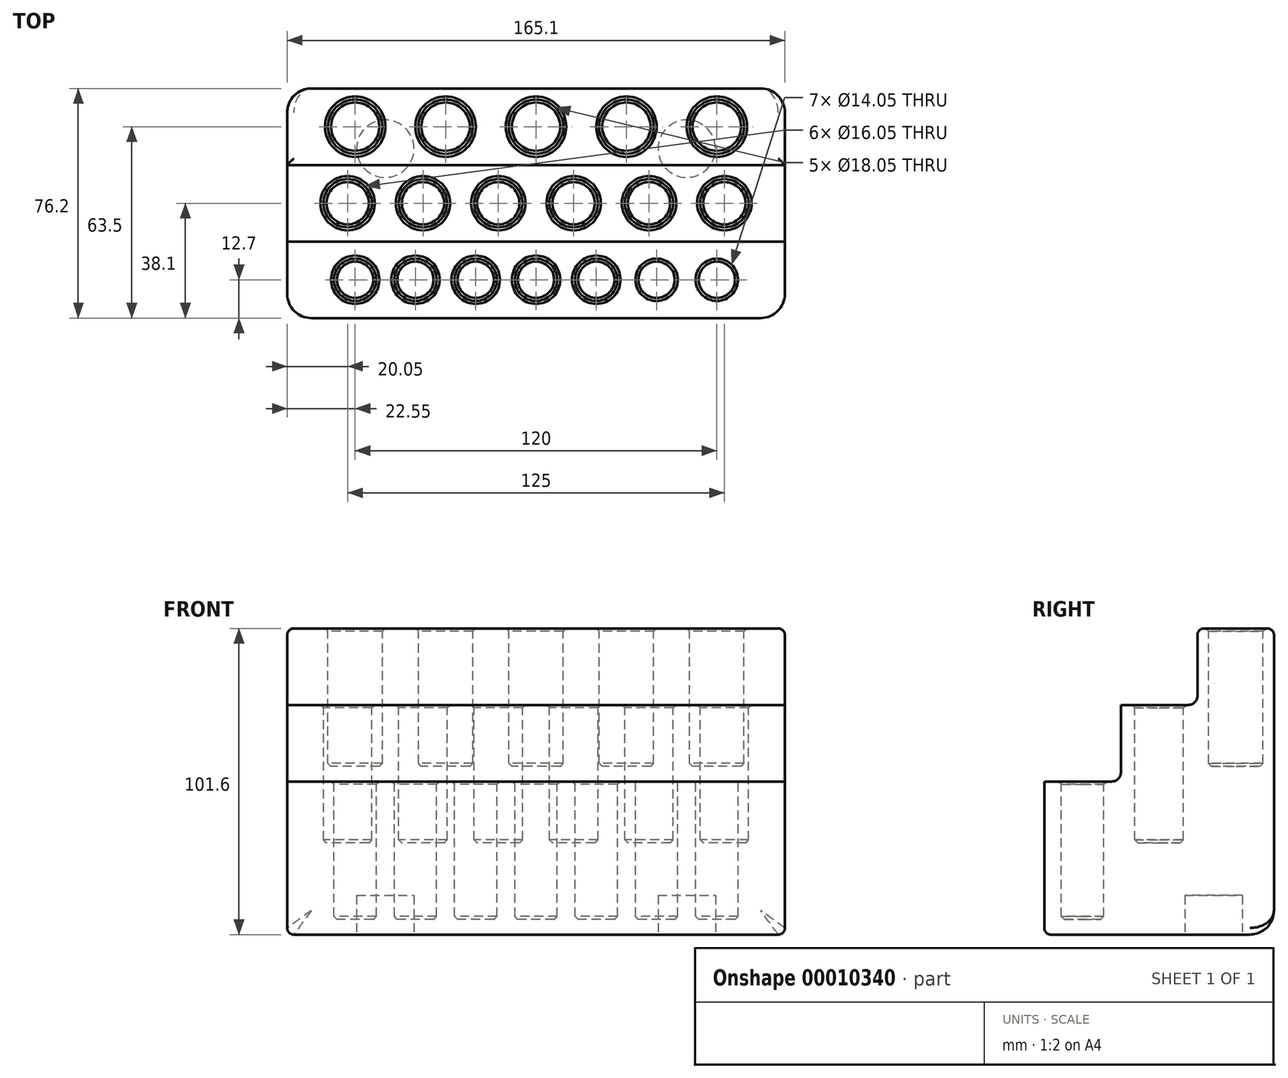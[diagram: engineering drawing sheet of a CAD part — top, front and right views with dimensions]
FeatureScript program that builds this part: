
annotation { "Feature Type Name" : "Feature", "Feature Type Description" : "" }
export const myFeature = defineFeature(function(context is Context, id is Id, definition is map)
    precondition{}
    {
        {
            var Q0;
            Q0=qCreatedBy(makeId("Top.planeOp"),FACE);
            var sketch = newSketch(context, id + "F0", { "sketchPlane" : qUnion([Q0])});
            skLineSegment(sketch, "E0.bottom", {"start": v(-77.55, 38.1) * mm, "end": v(77.55, 38.1) * mm});
            skLineSegment(sketch, "E0.top", {"start": v(-77.55, -38.1) * mm, "end": v(77.55, -38.1) * mm});
            skLineSegment(sketch, "E0.left", {"start": v(-82.55, 33.1) * mm, "end": v(-82.55, -33.1) * mm});
            skLineSegment(sketch, "E0.right", {"start": v(82.55, 33.1) * mm, "end": v(82.55, -33.1) * mm});
            skPoint(sketch, "E1.visualSharp", {"position": v(-82.55, 38.1) * mm});
            skPoint(sketch, "E2.visualSharp", {"position": v(82.55, -38.1) * mm});
            skPoint(sketch, "E3.visualSharp", {"position": v(-82.55, -38.1) * mm});
            skLineSegment(sketch, "E4", {"start": v(0, 38.1) * mm, "end": v(0, -38.1) * mm});
            skLineSegment(sketch, "E5", {"start": v(0, -38.1) * mm, "end": v(0, 0) * mm});
            skLineSegment(sketch, "E6", {"start": v(-82.55, 0) * mm, "end": v(0, 0) * mm});
            skLineSegment(sketch, "E7", {"start": v(82.55, 0) * mm, "end": v(0, 0) * mm});
            skLineSegment(sketch, "E8", {"start": v(-82.55, 33.1) * mm, "end": v(-82.55, 38.1) * mm});
            skLineSegment(sketch, "E9", {"start": v(-77.55, 38.1) * mm, "end": v(-82.55, 38.1) * mm});
            skLineSegment(sketch, "E10", {"start": v(77.55, 38.1) * mm, "end": v(82.55, 38.1) * mm});
            skLineSegment(sketch, "E11", {"start": v(82.55, 33.1) * mm, "end": v(82.55, 38.1) * mm});
            skLineSegment(sketch, "E12", {"start": v(-82.55, -33.1) * mm, "end": v(-82.55, -38.1) * mm});
            skLineSegment(sketch, "E13", {"start": v(-82.55, -38.1) * mm, "end": v(-77.55, -38.1) * mm});
            skLineSegment(sketch, "E14", {"start": v(82.55, -33.1) * mm, "end": v(82.55, -38.1) * mm});
            skLineSegment(sketch, "E15", {"start": v(77.55, -38.1) * mm, "end": v(82.55, -38.1) * mm});
            skSolve(sketch);
        }
        {
            var Q0;
            Q0 = qSketchRegion(id + "F0", true);
            extrude(context, id + "F1", {"entities" : qUnion([Q0]), "depth" : 101.6 * mm});
        }
        {
            var Q0;
            Q0=makeQuery(id+"F1.opExtrude","CAP_FACE",FACE,{"disambiguationData":[OSD([sQuery(id+"F0.wireOp",EDGE,"E0.bottom"),sQuery(id+"F0.wireOp",EDGE,"E0.top"),sQuery(id+"F0.wireOp",EDGE,"E0.left"),sQuery(id+"F0.wireOp",EDGE,"E0.right"),sQuery(id+"F0.wireOp",EDGE,"E1.filletArc"),sQuery(id+"F0.wireOp",EDGE,"520365cf-ff0a-4958-9614-1212a4c49a2f.filletArc"),sQuery(id+"F0.wireOp",EDGE,"E2.filletArc"),sQuery(id+"F0.wireOp",EDGE,"E3.filletArc")])],"isStart":false});
            var sketch = newSketch(context, id + "F2", { "sketchPlane" : qUnion([Q0])});
            skLineSegment(sketch, "E16.top", {"start": v(-82.55, 12.7) * mm, "end": v(82.55, 12.7) * mm});
            skLineSegment(sketch, "E17.top", {"start": v(-82.55, -12.7) * mm, "end": v(82.55, -12.7) * mm});
            skLineSegment(sketch, "E17.left", {"start": v(-82.55, 12.7) * mm, "end": v(-82.55, -12.7) * mm});
            skLineSegment(sketch, "E17.right", {"start": v(82.55, 12.7) * mm, "end": v(82.55, -12.7) * mm});
            skLineSegment(sketch, "E18.bottom", {"start": v(-82.55, 38.1) * mm, "end": v(82.55, 38.1) * mm});
            skLineSegment(sketch, "E18.left", {"start": v(-82.55, 38.1) * mm, "end": v(-82.55, 12.7) * mm});
            skLineSegment(sketch, "E18.right", {"start": v(82.55, 38.1) * mm, "end": v(82.55, 12.7) * mm});
            skLineSegment(sketch, "E19.top", {"start": v(-82.55, -38.1) * mm, "end": v(82.55, -38.1) * mm});
            skLineSegment(sketch, "E19.left", {"start": v(-82.55, -12.7) * mm, "end": v(-82.55, -38.1) * mm});
            skLineSegment(sketch, "E19.right", {"start": v(82.55, -12.7) * mm, "end": v(82.55, -38.1) * mm});
            skSolve(sketch);
        }
        {
            var Q0;
            Q0=makeQuery(id+"F2.imprint","IMPRINT",FACE,{"disambiguationData":[TD([[makeQuery(id+"F2.imprint","IMPRINT",EDGE,{"derivedFrom":sQuery(id+"F2.wireOp",EDGE,"E17.left")}),-1.0]])]});
            extrude(context, id + "F3", {"entities" : qUnion([Q0]), "operationType" : NewBodyOperationType.REMOVE, "oppositeDirection" : true, "depth" : 25.4 * mm});
        }
        {
            var Q0;
            {var subQ0=sQuery(id+"F0.wireOp",EDGE,"E0.top");var subQ1=sQuery(id+"F0.wireOp",EDGE,"E0.left");var subQ2=sQuery(id+"F0.wireOp",EDGE,"E0.right");var subQ3=sQuery(id+"F0.wireOp",EDGE,"E8");var subQ4=sQuery(id+"F0.wireOp",EDGE,"E11");var subQ5=sQuery(id+"F0.wireOp",EDGE,"E12");var subQ6=sQuery(id+"F0.wireOp",EDGE,"E13");var subQ7=sQuery(id+"F0.wireOp",EDGE,"E14");var subQ8=sQuery(id+"F0.wireOp",EDGE,"E15");Q0=makeQuery(id+"F3.boolean.opBoolean","SPLIT",FACE,{"disambiguationData":[TD([makeQuery(id+"F3.opExtrude","SWEPT_FACE",FACE,{"disambiguationData":[OSD([sQuery(id+"F2.wireOp",EDGE,"E17.top")])]})])],"derivedFrom":makeQuery(id+"F1.opExtrude","CAP_FACE",FACE,{"disambiguationData":[OSD([sQuery(id+"F0.wireOp",EDGE,"E0.bottom"),subQ0,subQ1,subQ2,subQ3,sQuery(id+"F0.wireOp",EDGE,"E9"),sQuery(id+"F0.wireOp",EDGE,"E10"),subQ4,subQ5,subQ6,subQ7,subQ8])],"isStart":false})});}
            extrude(context, id + "F4", {"entities" : qUnion([Q0]), "operationType" : NewBodyOperationType.REMOVE, "oppositeDirection" : true, "depth" : 50.8 * mm});
        }
        {
            var Q0;
            {var subQ0=sQuery(id+"F0.wireOp",EDGE,"E0.bottom");var subQ1=sQuery(id+"F0.wireOp",EDGE,"E0.left");var subQ2=sQuery(id+"F0.wireOp",EDGE,"E0.right");var subQ3=sQuery(id+"F0.wireOp",EDGE,"E8");var subQ4=sQuery(id+"F0.wireOp",EDGE,"E9");var subQ5=sQuery(id+"F0.wireOp",EDGE,"E10");var subQ6=sQuery(id+"F0.wireOp",EDGE,"E11");var subQ7=sQuery(id+"F0.wireOp",EDGE,"E12");var subQ8=sQuery(id+"F0.wireOp",EDGE,"E14");Q0=makeQuery(id+"F3.boolean.opBoolean","SPLIT",FACE,{"disambiguationData":[TD([makeQuery(id+"F3.opExtrude","SWEPT_FACE",FACE,{"disambiguationData":[OSD([sQuery(id+"F2.wireOp",EDGE,"E16.top")])]})])],"derivedFrom":makeQuery(id+"F1.opExtrude","CAP_FACE",FACE,{"disambiguationData":[OSD([subQ0,sQuery(id+"F0.wireOp",EDGE,"E0.top"),subQ1,subQ2,subQ3,subQ4,subQ5,subQ6,subQ7,sQuery(id+"F0.wireOp",EDGE,"E13"),subQ8,sQuery(id+"F0.wireOp",EDGE,"E15")])],"isStart":false})});}
            var sketch = newSketch(context, id + "F5", { "sketchPlane" : qUnion([Q0])});
            skCircle(sketch, "E20", {"center": v(-60, 25.4) * mm, "radius": 9.03 * mm});
            skCircle(sketch, "E21.1.0.0", {"center": v(-30, 25.4) * mm, "radius": 9.03 * mm});
            skCircle(sketch, "E21.2.0.0", {"center": v(0, 25.4) * mm, "radius": 9.03 * mm});
            skCircle(sketch, "E21.3.0.0", {"center": v(30, 25.4) * mm, "radius": 9.03 * mm});
            skLineSegment(sketch, "E21.direction1", {"start": v(-60, 25.4) * mm, "end": v(-30, 25.4) * mm, "construction": true});
            skCircle(sketch, "E22.0.4.0", {"center": v(60, 25.4) * mm, "radius": 9.03 * mm});
            skSolve(sketch);
        }
        {
            var Q0;
            Q0=makeQuery(id+"F5.imprint","IMPRINT",FACE,{"disambiguationData":[TD([[makeQuery(id+"F5.imprint","IMPRINT",EDGE,{"derivedFrom":sQuery(id+"F5.wireOp",EDGE,"E20")}),1.0]])]});
            var Q1;
            Q1=makeQuery(id+"F5.imprint","IMPRINT",FACE,{"disambiguationData":[TD([[makeQuery(id+"F5.imprint","IMPRINT",EDGE,{"derivedFrom":sQuery(id+"F5.wireOp",EDGE,"E21.1.0.0")}),1.0]])]});
            var Q2;
            Q2=makeQuery(id+"F5.imprint","IMPRINT",FACE,{"disambiguationData":[TD([[makeQuery(id+"F5.imprint","IMPRINT",EDGE,{"derivedFrom":sQuery(id+"F5.wireOp",EDGE,"E21.2.0.0")}),1.0]])]});
            var Q3;
            Q3=makeQuery(id+"F5.imprint","IMPRINT",FACE,{"disambiguationData":[TD([[makeQuery(id+"F5.imprint","IMPRINT",EDGE,{"derivedFrom":sQuery(id+"F5.wireOp",EDGE,"E21.3.0.0")}),1.0]])]});
            var Q4;
            Q4=makeQuery(id+"F5.imprint","IMPRINT",FACE,{"disambiguationData":[TD([[makeQuery(id+"F5.imprint","IMPRINT",EDGE,{"derivedFrom":sQuery(id+"F5.wireOp",EDGE,"E22.0.4.0")}),1.0]])]});
            extrude(context, id + "F6", {"entities" : qUnion([Q0, Q1, Q2, Q3, Q4]), "operationType" : NewBodyOperationType.REMOVE, "oppositeDirection" : true, "depth" : 45.8 * mm});
        }
        {
            var Q0;
            Q0=makeQuery(id+"F3.boolean.opBoolean","COPY",FACE,{"derivedFrom":makeQuery(id+"F3.opExtrude","CAP_FACE",FACE,{"disambiguationData":[OSD([sQuery(id+"F2.wireOp",EDGE,"E17.left"),sQuery(id+"F2.wireOp",EDGE,"E17.right"),sQuery(id+"F2.wireOp",EDGE,"E16.top"),sQuery(id+"F2.wireOp",EDGE,"E17.top")])],"isStart":false})});
            var sketch = newSketch(context, id + "F7", { "sketchPlane" : qUnion([Q0])});
            skCircle(sketch, "E23", {"center": v(-62.5, 0) * mm, "radius": 8.03 * mm});
            skCircle(sketch, "E24.1.0.0", {"center": v(-37.5, 0) * mm, "radius": 8.03 * mm});
            skCircle(sketch, "E24.2.0.0", {"center": v(-12.5, 0) * mm, "radius": 8.03 * mm});
            skCircle(sketch, "E24.3.0.0", {"center": v(12.5, 0) * mm, "radius": 8.03 * mm});
            skCircle(sketch, "E24.4.0.0", {"center": v(37.5, 0) * mm, "radius": 8.03 * mm});
            skCircle(sketch, "E24.5.0.0", {"center": v(62.5, 0) * mm, "radius": 8.03 * mm});
            skLineSegment(sketch, "E24.direction1", {"start": v(-62.5, 0) * mm, "end": v(-37.5, 0) * mm, "construction": true});
            skSolve(sketch);
        }
        {
            var Q0;
            Q0 = qSketchRegion(id + "F7", true);
            extrude(context, id + "F8", {"entities" : qUnion([Q0]), "operationType" : NewBodyOperationType.REMOVE, "oppositeDirection" : true, "depth" : 45.8 * mm});
        }
        {
            var Q0;
            Q0=makeQuery(id+"F4.boolean.opBoolean","COPY",FACE,{"derivedFrom":makeQuery(id+"F4.opExtrude","CAP_FACE",FACE,{"disambiguationData":[OSD([sQuery(id+"F0.wireOp",EDGE,"E0.bottom"),sQuery(id+"F0.wireOp",EDGE,"E0.top"),sQuery(id+"F0.wireOp",EDGE,"E0.left"),sQuery(id+"F0.wireOp",EDGE,"E0.right"),sQuery(id+"F0.wireOp",EDGE,"E8"),sQuery(id+"F0.wireOp",EDGE,"E9"),sQuery(id+"F0.wireOp",EDGE,"E10"),sQuery(id+"F0.wireOp",EDGE,"E11"),sQuery(id+"F0.wireOp",EDGE,"E12"),sQuery(id+"F0.wireOp",EDGE,"E13"),sQuery(id+"F0.wireOp",EDGE,"E14"),sQuery(id+"F0.wireOp",EDGE,"E15")])],"isStart":false})});
            var sketch = newSketch(context, id + "F9", { "sketchPlane" : qUnion([Q0])});
            skCircle(sketch, "E25", {"center": v(-60, -25.4) * mm, "radius": 7.03 * mm});
            skCircle(sketch, "E26.1.0.0", {"center": v(-40, -25.4) * mm, "radius": 7.03 * mm});
            skCircle(sketch, "E26.2.0.0", {"center": v(-20, -25.4) * mm, "radius": 7.03 * mm});
            skCircle(sketch, "E26.3.0.0", {"center": v(0, -25.4) * mm, "radius": 7.03 * mm});
            skCircle(sketch, "E26.4.0.0", {"center": v(20, -25.4) * mm, "radius": 7.03 * mm});
            skCircle(sketch, "E26.5.0.0", {"center": v(40, -25.4) * mm, "radius": 7.03 * mm});
            skCircle(sketch, "E26.6.0.0", {"center": v(60, -25.4) * mm, "radius": 7.03 * mm});
            skLineSegment(sketch, "E26.direction1", {"start": v(-60, -25.4) * mm, "end": v(-40, -25.4) * mm, "construction": true});
            skSolve(sketch);
        }
        {
            var Q0;
            Q0 = qSketchRegion(id + "F9", true);
            extrude(context, id + "F10", {"entities" : qUnion([Q0]), "operationType" : NewBodyOperationType.REMOVE, "oppositeDirection" : true, "depth" : 45.8 * mm});
        }
        {
            var Q0;
            Q0=makeQuery(id+"F1.opExtrude","CAP_FACE",FACE,{"disambiguationData":[OSD([sQuery(id+"F0.wireOp",EDGE,"E0.bottom"),sQuery(id+"F0.wireOp",EDGE,"E0.top"),sQuery(id+"F0.wireOp",EDGE,"E0.left"),sQuery(id+"F0.wireOp",EDGE,"E0.right"),sQuery(id+"F0.wireOp",EDGE,"E8"),sQuery(id+"F0.wireOp",EDGE,"E9"),sQuery(id+"F0.wireOp",EDGE,"E10"),sQuery(id+"F0.wireOp",EDGE,"E11"),sQuery(id+"F0.wireOp",EDGE,"E12"),sQuery(id+"F0.wireOp",EDGE,"E13"),sQuery(id+"F0.wireOp",EDGE,"E14"),sQuery(id+"F0.wireOp",EDGE,"E15")])],"isStart":true});
            var sketch = newSketch(context, id + "F11", { "sketchPlane" : qUnion([Q0])});
            skCircle(sketch, "E27", {"center": v(-50, -18.1) * mm, "radius": 9.53 * mm});
            skCircle(sketch, "E28", {"center": v(50, -18.1) * mm, "radius": 9.53 * mm});
            skLineSegment(sketch, "E29", {"start": v(0, 0) * mm, "end": v(0, -38.1) * mm});
            skSolve(sketch);
        }
        {
            var Q0;
            Q0 = qSketchRegion(id + "F11", true);
            extrude(context, id + "F12", {"entities" : qUnion([Q0]), "operationType" : NewBodyOperationType.REMOVE, "oppositeDirection" : true, "depth" : 13 * mm});
        }
        {
            var Q0;
            {var subQ0=sQuery(id+"F0.wireOp",EDGE,"E0.left");var subQ1=sQuery(id+"F0.wireOp",EDGE,"E8");var subQ2=sQuery(id+"F0.wireOp",EDGE,"E12");Q0=makeQuery(id+"F3.boolean.opBoolean","SPLIT",EDGE,{"disambiguationData":[TD([makeQuery(id+"F3.opExtrude","SWEPT_FACE",FACE,{"disambiguationData":[OSD([sQuery(id+"F2.wireOp",EDGE,"E16.top")])]})])],"derivedFrom":makeQuery(id+"F1.opExtrude","CAP_EDGE",EDGE,{"disambiguationData":[OSD([subQ0,subQ1,subQ2])],"isStart":false})});}
            var Q1;
            Q1=makeQuery(id+"F1.opExtrude","CAP_EDGE",EDGE,{"disambiguationData":[OSD([sQuery(id+"F0.wireOp",EDGE,"E0.bottom"),sQuery(id+"F0.wireOp",EDGE,"E9"),sQuery(id+"F0.wireOp",EDGE,"E10")])],"isStart":false});
            var Q2;
            {var subQ0=sQuery(id+"F0.wireOp",EDGE,"E0.right");var subQ1=sQuery(id+"F0.wireOp",EDGE,"E11");var subQ2=sQuery(id+"F0.wireOp",EDGE,"E14");Q2=makeQuery(id+"F3.boolean.opBoolean","SPLIT",EDGE,{"disambiguationData":[TD([makeQuery(id+"F3.opExtrude","SWEPT_FACE",FACE,{"disambiguationData":[OSD([sQuery(id+"F2.wireOp",EDGE,"E16.top")])]})])],"derivedFrom":makeQuery(id+"F1.opExtrude","CAP_EDGE",EDGE,{"disambiguationData":[OSD([subQ0,subQ1,subQ2])],"isStart":false})});}
            var Q3;
            Q3=makeQuery(id+"F3.boolean.opBoolean","COPY",EDGE,{"derivedFrom":makeQuery(id+"F3.opExtrude","CAP_EDGE",EDGE,{"disambiguationData":[OSD([sQuery(id+"F2.wireOp",EDGE,"E16.top")])],"isStart":true})});
            var Q4;
            Q4=makeQuery(id+"F3.boolean.opBoolean","COPY",EDGE,{"derivedFrom":makeQuery(id+"F3.opExtrude","CAP_EDGE",EDGE,{"disambiguationData":[OSD([sQuery(id+"F2.wireOp",EDGE,"E17.right")])],"isStart":false})});
            var Q5;
            Q5=makeQuery(id+"F3.boolean.opBoolean","COPY",EDGE,{"derivedFrom":makeQuery(id+"F3.opExtrude","CAP_EDGE",EDGE,{"disambiguationData":[OSD([sQuery(id+"F2.wireOp",EDGE,"E17.top")])],"isStart":false})});
            var Q6;
            Q6=makeQuery(id+"F3.boolean.opBoolean","COPY",EDGE,{"derivedFrom":makeQuery(id+"F3.opExtrude","CAP_EDGE",EDGE,{"disambiguationData":[OSD([sQuery(id+"F2.wireOp",EDGE,"E17.left")])],"isStart":false})});
            var Q7;
            Q7=makeQuery(id+"F4.boolean.opBoolean","COPY",EDGE,{"derivedFrom":makeQuery(id+"F4.opExtrude","CAP_EDGE",EDGE,{"disambiguationData":[OSD([sQuery(id+"F0.wireOp",EDGE,"E0.left"),sQuery(id+"F0.wireOp",EDGE,"E8"),sQuery(id+"F0.wireOp",EDGE,"E12")])],"isStart":false})});
            var Q8;
            Q8=makeQuery(id+"F4.boolean.opBoolean","COPY",EDGE,{"derivedFrom":makeQuery(id+"F4.opExtrude","CAP_EDGE",EDGE,{"disambiguationData":[OSD([sQuery(id+"F0.wireOp",EDGE,"E0.top"),sQuery(id+"F0.wireOp",EDGE,"E13"),sQuery(id+"F0.wireOp",EDGE,"E15")])],"isStart":false})});
            var Q9;
            Q9=makeQuery(id+"F4.boolean.opBoolean","COPY",EDGE,{"derivedFrom":makeQuery(id+"F4.opExtrude","CAP_EDGE",EDGE,{"disambiguationData":[OSD([sQuery(id+"F0.wireOp",EDGE,"E0.right"),sQuery(id+"F0.wireOp",EDGE,"E11"),sQuery(id+"F0.wireOp",EDGE,"E14")])],"isStart":false})});
            var Q10;
            Q10=makeQuery(id+"F1.opExtrude","CAP_EDGE",EDGE,{"disambiguationData":[OSD([sQuery(id+"F0.wireOp",EDGE,"E0.top"),sQuery(id+"F0.wireOp",EDGE,"E13"),sQuery(id+"F0.wireOp",EDGE,"E15")])],"isStart":true});
            var Q11;
            Q11=makeQuery(id+"F1.opExtrude","CAP_EDGE",EDGE,{"disambiguationData":[OSD([sQuery(id+"F0.wireOp",EDGE,"E0.left"),sQuery(id+"F0.wireOp",EDGE,"E8"),sQuery(id+"F0.wireOp",EDGE,"E12")])],"isStart":true});
            var Q12;
            Q12=makeQuery(id+"F1.opExtrude","CAP_EDGE",EDGE,{"disambiguationData":[OSD([sQuery(id+"F0.wireOp",EDGE,"E0.right"),sQuery(id+"F0.wireOp",EDGE,"E11"),sQuery(id+"F0.wireOp",EDGE,"E14")])],"isStart":true});
            fillet(context, id + "F13", {"entities" : qUnion([Q0, Q1, Q2, Q3, Q4, Q5, Q6, Q7, Q8, Q9, Q10, Q11, Q12]), "radius" : 2.2 * mm, "tangentPropagation" : true, "allowEdgeOverflow" : false});
        }
        {
            var Q0;
            Q0=makeQuery(id+"F6.boolean.opBoolean","COPY",FACE,{"derivedFrom":makeQuery(id+"F6.opExtrude","SWEPT_FACE",FACE,{"disambiguationData":[OSD([sQuery(id+"F5.wireOp",EDGE,"E20")])]})});
            var Q1;
            Q1=makeQuery(id+"F6.boolean.opBoolean","COPY",FACE,{"derivedFrom":makeQuery(id+"F6.opExtrude","SWEPT_FACE",FACE,{"disambiguationData":[OSD([sQuery(id+"F5.wireOp",EDGE,"E21.1.0.0")])]})});
            var Q2;
            Q2=makeQuery(id+"F6.boolean.opBoolean","COPY",FACE,{"derivedFrom":makeQuery(id+"F6.opExtrude","SWEPT_FACE",FACE,{"disambiguationData":[OSD([sQuery(id+"F5.wireOp",EDGE,"E21.2.0.0")])]})});
            var Q3;
            Q3=makeQuery(id+"F6.boolean.opBoolean","COPY",FACE,{"derivedFrom":makeQuery(id+"F6.opExtrude","SWEPT_FACE",FACE,{"disambiguationData":[OSD([sQuery(id+"F5.wireOp",EDGE,"E21.3.0.0")])]})});
            var Q4;
            Q4=makeQuery(id+"F6.boolean.opBoolean","COPY",FACE,{"derivedFrom":makeQuery(id+"F6.opExtrude","SWEPT_FACE",FACE,{"disambiguationData":[OSD([sQuery(id+"F5.wireOp",EDGE,"E22.0.4.0")])]})});
            var Q5;
            Q5=makeQuery(id+"F8.boolean.opBoolean","COPY",FACE,{"derivedFrom":makeQuery(id+"F8.opExtrude","SWEPT_FACE",FACE,{"disambiguationData":[OSD([sQuery(id+"F7.wireOp",EDGE,"E24.5.0.0")])]})});
            var Q6;
            Q6=makeQuery(id+"F8.boolean.opBoolean","COPY",FACE,{"derivedFrom":makeQuery(id+"F8.opExtrude","SWEPT_FACE",FACE,{"disambiguationData":[OSD([sQuery(id+"F7.wireOp",EDGE,"E24.4.0.0")])]})});
            var Q7;
            Q7=makeQuery(id+"F8.boolean.opBoolean","COPY",FACE,{"derivedFrom":makeQuery(id+"F8.opExtrude","SWEPT_FACE",FACE,{"disambiguationData":[OSD([sQuery(id+"F7.wireOp",EDGE,"E24.3.0.0")])]})});
            var Q8;
            Q8=makeQuery(id+"F8.boolean.opBoolean","COPY",FACE,{"derivedFrom":makeQuery(id+"F8.opExtrude","SWEPT_FACE",FACE,{"disambiguationData":[OSD([sQuery(id+"F7.wireOp",EDGE,"E24.2.0.0")])]})});
            var Q9;
            Q9=makeQuery(id+"F8.boolean.opBoolean","COPY",FACE,{"derivedFrom":makeQuery(id+"F8.opExtrude","SWEPT_FACE",FACE,{"disambiguationData":[OSD([sQuery(id+"F7.wireOp",EDGE,"E24.1.0.0")])]})});
            var Q10;
            Q10=makeQuery(id+"F8.boolean.opBoolean","COPY",FACE,{"derivedFrom":makeQuery(id+"F8.opExtrude","SWEPT_FACE",FACE,{"disambiguationData":[OSD([sQuery(id+"F7.wireOp",EDGE,"E23")])]})});
            var Q11;
            Q11=makeQuery(id+"F10.boolean.opBoolean","COPY",FACE,{"derivedFrom":makeQuery(id+"F10.opExtrude","SWEPT_FACE",FACE,{"disambiguationData":[OSD([sQuery(id+"F9.wireOp",EDGE,"E25")])]})});
            var Q12;
            Q12=makeQuery(id+"F10.boolean.opBoolean","COPY",FACE,{"derivedFrom":makeQuery(id+"F10.opExtrude","SWEPT_FACE",FACE,{"disambiguationData":[OSD([sQuery(id+"F9.wireOp",EDGE,"E26.1.0.0")])]})});
            var Q13;
            Q13=makeQuery(id+"F10.boolean.opBoolean","COPY",FACE,{"derivedFrom":makeQuery(id+"F10.opExtrude","SWEPT_FACE",FACE,{"disambiguationData":[OSD([sQuery(id+"F9.wireOp",EDGE,"E26.2.0.0")])]})});
            var Q14;
            Q14=makeQuery(id+"F10.boolean.opBoolean","COPY",FACE,{"derivedFrom":makeQuery(id+"F10.opExtrude","SWEPT_FACE",FACE,{"disambiguationData":[OSD([sQuery(id+"F9.wireOp",EDGE,"E26.3.0.0")])]})});
            var Q15;
            Q15=makeQuery(id+"F10.boolean.opBoolean","COPY",FACE,{"derivedFrom":makeQuery(id+"F10.opExtrude","SWEPT_FACE",FACE,{"disambiguationData":[OSD([sQuery(id+"F9.wireOp",EDGE,"E26.4.0.0")])]})});
            var Q16;
            Q16=makeQuery(id+"F10.boolean.opBoolean","COPY",EDGE,{"derivedFrom":makeQuery(id+"F10.opExtrude","CAP_EDGE",EDGE,{"disambiguationData":[OSD([sQuery(id+"F9.wireOp",EDGE,"E26.6.0.0")])],"isStart":true})});
            var Q17;
            Q17=makeQuery(id+"F10.boolean.opBoolean","COPY",EDGE,{"derivedFrom":makeQuery(id+"F10.opExtrude","CAP_EDGE",EDGE,{"disambiguationData":[OSD([sQuery(id+"F9.wireOp",EDGE,"E26.5.0.0")])],"isStart":true})});
            var Q18;
            Q18=makeQuery(id+"F10.boolean.opBoolean","COPY",FACE,{"derivedFrom":makeQuery(id+"F10.opExtrude","CAP_FACE",FACE,{"disambiguationData":[OSD([sQuery(id+"F9.wireOp",EDGE,"E26.5.0.0")])],"isStart":false})});
            var Q19;
            Q19=makeQuery(id+"F10.boolean.opBoolean","COPY",FACE,{"derivedFrom":makeQuery(id+"F10.opExtrude","CAP_FACE",FACE,{"disambiguationData":[OSD([sQuery(id+"F9.wireOp",EDGE,"E26.6.0.0")])],"isStart":false})});
            chamfer(context, id + "F14", {"entities" : qUnion([Q0, Q1, Q2, Q3, Q4, Q5, Q6, Q7, Q8, Q9, Q10, Q11, Q12, Q13, Q14, Q15, Q16, Q17, Q18, Q19]), "width" : 1 * mm, "tangentPropagation" : true});
        }
        {
            var Q0;
            Q0=makeQuery(id+"F1.opExtrude","SWEPT_EDGE",EDGE,{"disambiguationData":[OSD([sQuery(id+"F0.wireOp",EDGE,"E10"),sQuery(id+"F0.wireOp",EDGE,"E11")])]});
            var Q1;
            Q1=makeQuery(id+"F1.opExtrude","SWEPT_EDGE",EDGE,{"disambiguationData":[OSD([sQuery(id+"F0.wireOp",EDGE,"E14"),sQuery(id+"F0.wireOp",EDGE,"E15")])]});
            var Q2;
            Q2=makeQuery(id+"F1.opExtrude","SWEPT_EDGE",EDGE,{"disambiguationData":[OSD([sQuery(id+"F0.wireOp",EDGE,"E12"),sQuery(id+"F0.wireOp",EDGE,"E13")])]});
            var Q3;
            Q3=makeQuery(id+"F3.boolean.opBoolean","COPY",EDGE,{"derivedFrom":makeQuery(id+"F3.opExtrude","SWEPT_EDGE",EDGE,{"disambiguationData":[OSD([sQuery(id+"F2.wireOp",EDGE,"E17.left"),sQuery(id+"F2.wireOp",EDGE,"E16.top"),sQuery(id+"F2.wireOp",EDGE,"E18.left")])]})});
            var Q4;
            Q4=makeQuery(id+"F3.boolean.opBoolean","COPY",EDGE,{"derivedFrom":makeQuery(id+"F3.opExtrude","SWEPT_EDGE",EDGE,{"disambiguationData":[OSD([sQuery(id+"F2.wireOp",EDGE,"E17.right"),sQuery(id+"F2.wireOp",EDGE,"E16.top"),sQuery(id+"F2.wireOp",EDGE,"E18.right")])]})});
            var Q5;
            Q5=makeQuery(id+"F4.boolean.opBoolean","COPY",EDGE,{"derivedFrom":makeQuery(id+"F4.opExtrude","SWEPT_EDGE",EDGE,{"disambiguationData":[OSD([sQuery(id+"F2.wireOp",EDGE,"E17.right"),sQuery(id+"F2.wireOp",EDGE,"E17.top"),sQuery(id+"F2.wireOp",EDGE,"E19.right")])]})});
            var Q6;
            Q6=makeQuery(id+"F4.boolean.opBoolean","COPY",EDGE,{"derivedFrom":makeQuery(id+"F4.opExtrude","SWEPT_EDGE",EDGE,{"disambiguationData":[OSD([sQuery(id+"F2.wireOp",EDGE,"E17.left"),sQuery(id+"F2.wireOp",EDGE,"E17.top"),sQuery(id+"F2.wireOp",EDGE,"E19.left")])]})});
            fillet(context, id + "F15", {"entities" : qUnion([Q0, Q1, Q2, Q3, Q4, Q5, Q6]), "radius" : 8 * mm, "tangentPropagation" : true, "allowEdgeOverflow" : false});
        }
        {
            var Q0;
            Q0=makeQuery(id+"F3.boolean.opBoolean","COPY",EDGE,{"derivedFrom":makeQuery(id+"F3.opExtrude","CAP_EDGE",EDGE,{"disambiguationData":[OSD([sQuery(id+"F2.wireOp",EDGE,"E16.top")])],"isStart":false})});
            var Q1;
            Q1=makeQuery(id+"F4.boolean.opBoolean","COPY",EDGE,{"derivedFrom":makeQuery(id+"F4.opExtrude","CAP_EDGE",EDGE,{"disambiguationData":[OSD([sQuery(id+"F2.wireOp",EDGE,"E17.top")])],"isStart":false})});
            fillet(context, id + "F16", {"entities" : qUnion([Q0, Q1]), "radius" : 3 * mm, "tangentPropagation" : true, "allowEdgeOverflow" : false});
        }
    });
